# Revit family: Haworth_Cotone_OccasionalTable
name_source: partatom
category: Furniture
revit_build: Autodesk Revit 2018 (Build: 20170223_1515(x64)
units: mm (PartAtom-declared; Revit-internal decimal feet)

## family parameters
Always vertical = Yes
Cut with Voids When Loaded = No
OmniClass Number = 23.40.70.14.64.21
OmniClass Title = Systems Furniture
Room Calculation Point = No
Shared = No
Work Plane-Based = No

## types (5) — shared parameters
Assembly Code = E2020200
Custom Size = No
Description = Haworth - Cassina - Cotone - Occasional Table
Glide Finish = Haworth _ Polymer _ Black
Manufacturer = Haworth
Model = Haworth - Cassina - Cotone
Revision Number = 1
Size = Verify Final Dim. w/ Haworth
Sustainability Info = https://www.haworth.com
URL = https://www.haworth.com
URL - Product = https://www.haworth.com
Warranty = http://www.haworth.com

## per-type parameters (varying)
| type | 25.6w x 13.8d | 35.4w x 35.4d | 51.2w x 13.8d | 55.1w x 35.4d | Actual Depth | Actual Height | Actual Width | Depth | Extra Large | Extra Small | High | Large | Low | Medium | Small | Width |
| 55.1w x 35.4d x 12.4h | No | No | No | Yes | 35.4 " | 12.4 " | 55.1 " | 35.4 " | Yes | No | No | No | Yes | No | No | 55.1 " |
| 25.6w x 13.8d x 23.7h | Yes | No | No | No | 13.8 " | 23.7 " | 25.6 " | 13.8 " | No | Yes | Yes | No | No | No | No | 25.6 " |
| 35.4w x 35.4d x 12.4h | No | Yes | No | No | 35.4 " | 12.4 " | 35.4 " | 35.4 " | No | No | No | No | Yes | No | Yes | 35.4 " |
| 51.2w x 13.8d x 23.7h | No | No | Yes | No | 13.8 " | 23.7 " | 51.2 " | 13.8 " | No | No | Yes | Yes | No | No | No | 51.2 " |
| 25.6w x 13.8d x 15.8h | Yes | No | No | No | 13.8 " | 15.8 " | 25.6 " | 13.8 " | No | Yes | No | No | No | Yes | No | 25.6 " |

## geometry (parser evidence)
native form markers: Sweep x8
no freeform markers — native parametric forms only
